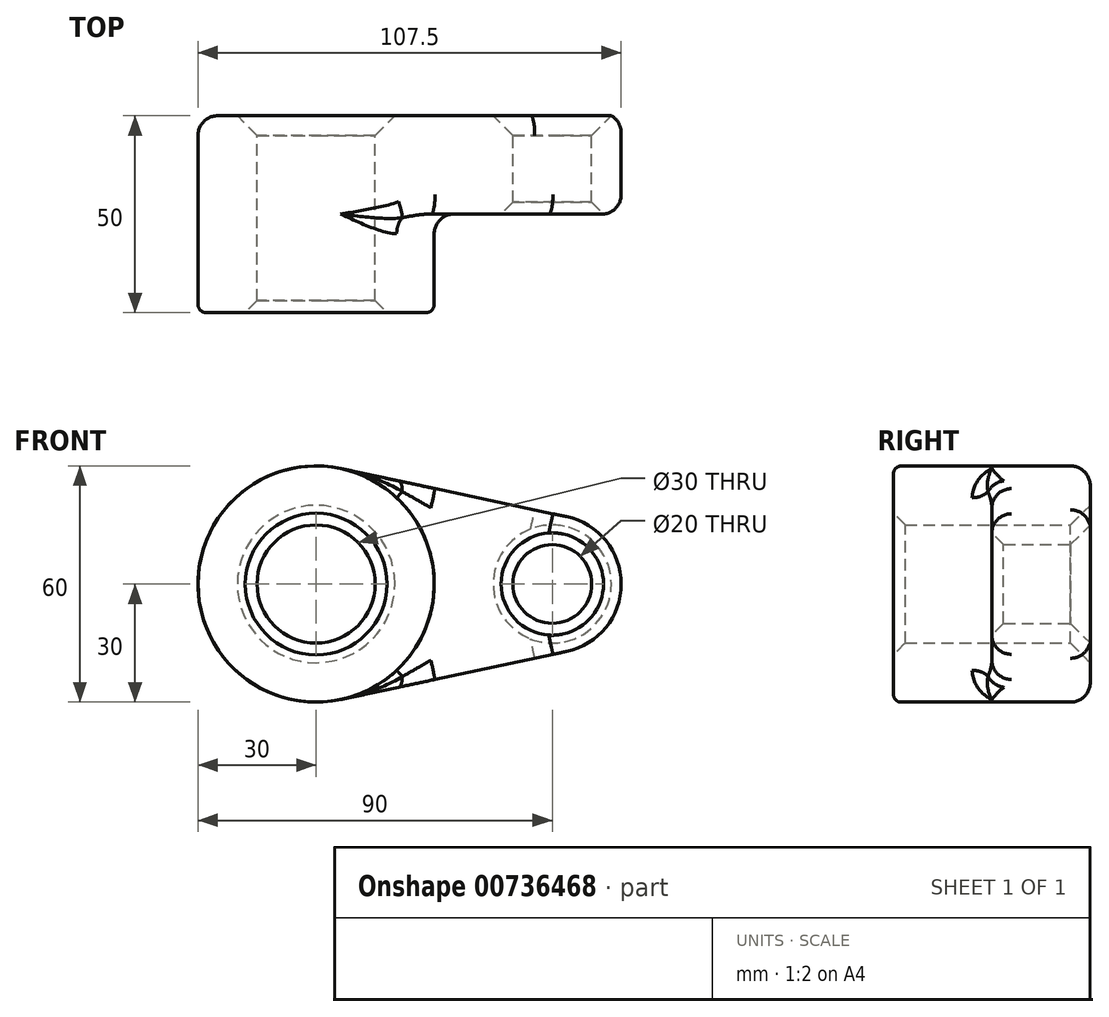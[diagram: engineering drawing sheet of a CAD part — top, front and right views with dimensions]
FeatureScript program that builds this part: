
annotation { "Feature Type Name" : "Feature", "Feature Type Description" : "" }
export const myFeature = defineFeature(function(context is Context, id is Id, definition is map)
    precondition{}
    {
        {
            var Q0;
            Q0=qCreatedBy(makeId("Front.planeOp"),FACE);
            var sketch = newSketch(context, id + "F0", { "sketchPlane" : qUnion([Q0])});
            skCircle(sketch, "E0", {"center": v(0, 0) * mm, "radius": 30 * mm});
            skCircle(sketch, "E1", {"center": v(60, 0) * mm, "radius": 17.5 * mm});
            skLineSegment(sketch, "E2", {"start": v(6.25, 29.34) * mm, "end": v(63.65, 17.12) * mm});
            skLineSegment(sketch, "E3", {"start": v(6.25, -29.34) * mm, "end": v(63.65, -17.12) * mm});
            skCircle(sketch, "E4", {"center": v(0, 0) * mm, "radius": 15 * mm});
            skCircle(sketch, "E5", {"center": v(60, 0) * mm, "radius": 10 * mm});
            skSolve(sketch);
        }
        {
            var Q0;
            Q0 = qSketchRegion(id + "F0", true);
            extrude(context, id + "F1", {"entities" : qUnion([Q0]), "depth" : 25 * mm, "offsetDistance" : 25 * mm});
        }
        {
            var Q0;
            Q0=makeQuery(id+"F0.imprint","IMPRINT",FACE,{"disambiguationData":[TD([[makeQuery(id+"F0.imprint","IMPRINT",EDGE,{"derivedFrom":sQuery(id+"F0.wireOp",EDGE,"E4")}),-1.0]])]});
            extrude(context, id + "F2", {"entities" : qUnion([Q0]), "operationType" : NewBodyOperationType.ADD, "depth" : 50 * mm, "offsetDistance" : 25 * mm});
        }
        {
            var Q0;
            Q0=makeQuery(id+"F2.opExtrude","CAP_EDGE",EDGE,{"disambiguationData":[OSD([sQuery(id+"F0.wireOp",EDGE,"E0")])],"isStart":false});
            fillet(context, id + "F3", {"entities" : qUnion([Q0]), "radius" : 2 * mm, "tangentPropagation" : true, "allowEdgeOverflow" : false});
        }
        {
            var Q0;
            Q0=makeQuery(id+"F2.opExtrude","CAP_EDGE",EDGE,{"disambiguationData":[OSD([sQuery(id+"F0.wireOp",EDGE,"E4")])],"isStart":false});
            var Q1;
            Q1=makeQuery(id+"F1.opExtrude","CAP_EDGE",EDGE,{"disambiguationData":[OSD([sQuery(id+"F0.wireOp",EDGE,"E5")])],"isStart":false});
            chamfer(context, id + "F4", {"entities" : qUnion([Q0, Q1]), "width" : 3 * mm, "tangentPropagation" : true});
        }
        {
            var Q0;
            {var subQ0=sQuery(id+"F0.wireOp",EDGE,"E0");Q0=makeQuery(id+"F2.boolean.opBoolean","INTERSECT",EDGE,{"derivedFrom":[makeQuery(id+"F1.opExtrude","CAP_FACE",FACE,{"disambiguationData":[OSD([subQ0,sQuery(id+"F0.wireOp",EDGE,"E1"),sQuery(id+"F0.wireOp",EDGE,"E2"),sQuery(id+"F0.wireOp",EDGE,"E3"),sQuery(id+"F0.wireOp",EDGE,"E4"),sQuery(id+"F0.wireOp",EDGE,"E5")])],"isStart":false}),makeQuery(id+"F2.opExtrude","SWEPT_FACE",FACE,{"disambiguationData":[OSD([subQ0])]})]});}
            fillet(context, id + "F5", {"entities" : qUnion([Q0]), "radius" : 5 * mm, "tangentPropagation" : true, "allowEdgeOverflow" : false});
        }
        {
            var Q0;
            Q0=makeQuery(id+"F1.opExtrude","CAP_EDGE",EDGE,{"disambiguationData":[OSD([sQuery(id+"F0.wireOp",EDGE,"E5")])],"isStart":true});
            var Q1;
            Q1=makeQuery(id+"F1.opExtrude","CAP_EDGE",EDGE,{"disambiguationData":[OSD([sQuery(id+"F0.wireOp",EDGE,"E4")])],"isStart":true});
            chamfer(context, id + "F6", {"entities" : qUnion([Q0, Q1]), "width" : 5 * mm, "tangentPropagation" : true});
        }
        {
            var Q0;
            Q0=makeQuery(id+"F1.opExtrude","CAP_EDGE",EDGE,{"disambiguationData":[OSD([sQuery(id+"F0.wireOp",EDGE,"E2")])],"isStart":false});
            var Q1;
            Q1=makeQuery(id+"F1.opExtrude","CAP_EDGE",EDGE,{"disambiguationData":[OSD([sQuery(id+"F0.wireOp",EDGE,"E2")])],"isStart":true});
            fillet(context, id + "F7", {"entities" : qUnion([Q0, Q1]), "radius" : 5 * mm, "tangentPropagation" : true, "allowEdgeOverflow" : false});
        }
    });
